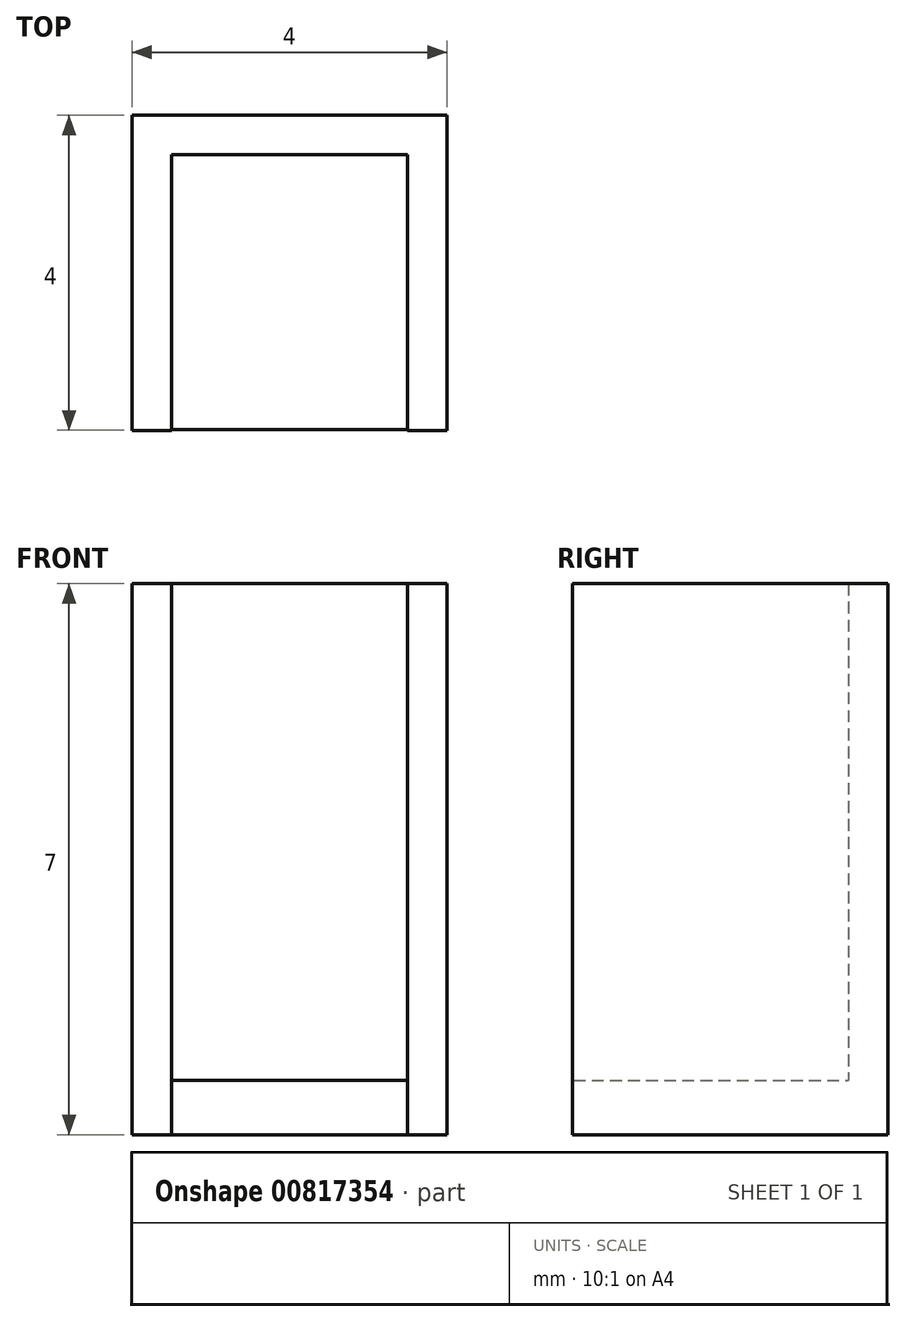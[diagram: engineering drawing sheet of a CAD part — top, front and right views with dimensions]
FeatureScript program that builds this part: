
annotation { "Feature Type Name" : "Feature", "Feature Type Description" : "" }
export const myFeature = defineFeature(function(context is Context, id is Id, definition is map)
    precondition{}
    {
        {
            var Q0;
            Q0=qCreatedBy(makeId("Top.planeOp"),FACE);
            var sketch = newSketch(context, id + "F0", { "sketchPlane" : qUnion([Q0])});
            skArc(sketch, "E0", {"start": v(-11, -10.87) * mm, "mid": v(0, -16.37) * mm, "end": v(11, -10.87) * mm});
            skLineSegment(sketch, "E1.right", {"start": v(-11, 5.63) * mm, "end": v(-11, -10.87) * mm});
            skLineSegment(sketch, "E2.right", {"start": v(11, 5.63) * mm, "end": v(11, -10.87) * mm});
            skArc(sketch, "E3.trimOffspring", {"start": v(11, 5.63) * mm, "mid": v(0, 11.13) * mm, "end": v(-11, 5.63) * mm});
            skArc(sketch, "E4", {"start": v(-2, 2.86) * mm, "mid": v(0, -13.9) * mm, "end": v(2, 2.86) * mm});
            skLineSegment(sketch, "E5.top", {"start": v(2, 6.86) * mm, "end": v(-2, 6.86) * mm});
            skLineSegment(sketch, "E5.right", {"start": v(-2, 2.86) * mm, "end": v(-2, 6.86) * mm});
            skLineSegment(sketch, "E6", {"start": v(2, 6.86) * mm, "end": v(2, 2.86) * mm});
            skSolve(sketch);
        }
        {
            var Q0;
            Q0=makeQuery(id+"F0.imprint","IMPRINT",FACE,{"disambiguationData":[TD([[makeQuery(id+"F0.imprint","IMPRINT",EDGE,{"derivedFrom":sQuery(id+"F0.wireOp",EDGE,"E0")}),1.0]])]});
            var sketch = newSketch(context, id + "F1", { "sketchPlane" : qUnion([Q0])});
            skLineSegment(sketch, "E7.bottom", {"start": v(-2, 6.86) * mm, "end": v(2, 6.86) * mm});
            skLineSegment(sketch, "E7.top", {"start": v(-2, 2.86) * mm, "end": v(-1.5, 2.86) * mm});
            skLineSegment(sketch, "E7.left", {"start": v(-2, 6.86) * mm, "end": v(-2, 2.86) * mm});
            skLineSegment(sketch, "E7.right", {"start": v(2, 6.86) * mm, "end": v(2, 2.86) * mm});
            skLineSegment(sketch, "E8.top", {"start": v(-2, 6.86) * mm, "end": v(-1.5, 6.86) * mm});
            skLineSegment(sketch, "E8.left", {"start": v(-2, 2.86) * mm, "end": v(-2, 6.86) * mm});
            skLineSegment(sketch, "E8.right", {"start": v(-1.5, 2.86) * mm, "end": v(-1.5, 6.36) * mm});
            skLineSegment(sketch, "E9.bottom", {"start": v(-1.5, 6.86) * mm, "end": v(2, 6.86) * mm});
            skLineSegment(sketch, "E9.top", {"start": v(-1.5, 6.36) * mm, "end": v(1.5, 6.36) * mm});
            skLineSegment(sketch, "E9.right", {"start": v(2, 6.86) * mm, "end": v(2, 6.36) * mm});
            skLineSegment(sketch, "E10.bottom", {"start": v(2, 6.86) * mm, "end": v(1.5, 6.86) * mm});
            skLineSegment(sketch, "E10.top", {"start": v(2, 2.86) * mm, "end": v(1.5, 2.86) * mm});
            skLineSegment(sketch, "E10.right", {"start": v(1.5, 6.36) * mm, "end": v(1.5, 2.86) * mm});
            skLineSegment(sketch, "E11.trimOffspring", {"start": v(1.5, 2.86) * mm, "end": v(2, 2.86) * mm});
            skSolve(sketch);
        }
        {
            var Q0;
            Q0=qSketchRegion(id+"F1",true);
            var Q1;
            {var subQ5=sQuery(id+"F1.wireOp",EDGE,"E7.top");Q1=makeQuery(id+"F1.imprint","IMPRINT",FACE,{"disambiguationData":[TD([[makeQuery(id+"F1.imprint","IMPRINT",EDGE,{"derivedFrom":subQ5}),1.0]])]});}
            extrude(context, id + "F2", {"entities" : qUnion([Q0, Q1]), "depth" : 7 * mm, "offsetDistance" : 25 * mm});
        }
        {
            var Q0;
            Q0=qCreatedBy(makeId("Front.planeOp"),FACE);
            cPlane(context, id + "F3", {"entities" : qUnion([Q0]), "cplaneType" : CPlaneType.OFFSET, "offset" : 6.5 * mm, "oppositeDirection" : true, "width" : 150 * mm, "height" : 150 * mm});
        }
        {
            var Q0;
            Q0=qCreatedBy(id+"F3.planeOp",FACE);
            var sketch = newSketch(context, id + "F4", { "sketchPlane" : qUnion([Q0])});
            skLineSegment(sketch, "E12.bottom", {"start": v(-1.5, 0) * mm, "end": v(1.5, 0) * mm});
            skLineSegment(sketch, "E12.top", {"start": v(-1.5, 0.69) * mm, "end": v(1.5, 0.69) * mm});
            skLineSegment(sketch, "E12.left", {"start": v(-1.5, 0) * mm, "end": v(-1.5, 0.69) * mm});
            skLineSegment(sketch, "E12.right", {"start": v(1.5, 0) * mm, "end": v(1.5, 0.69) * mm});
            skSolve(sketch);
        }
        {
            var Q0;
            Q0=qSketchRegion(id+"F4",true);
            extrude(context, id + "F5", {"entities" : qUnion([Q0]), "operationType" : NewBodyOperationType.ADD, "depth" : 3.63 * mm, "offsetDistance" : 25 * mm});
        }
    });
